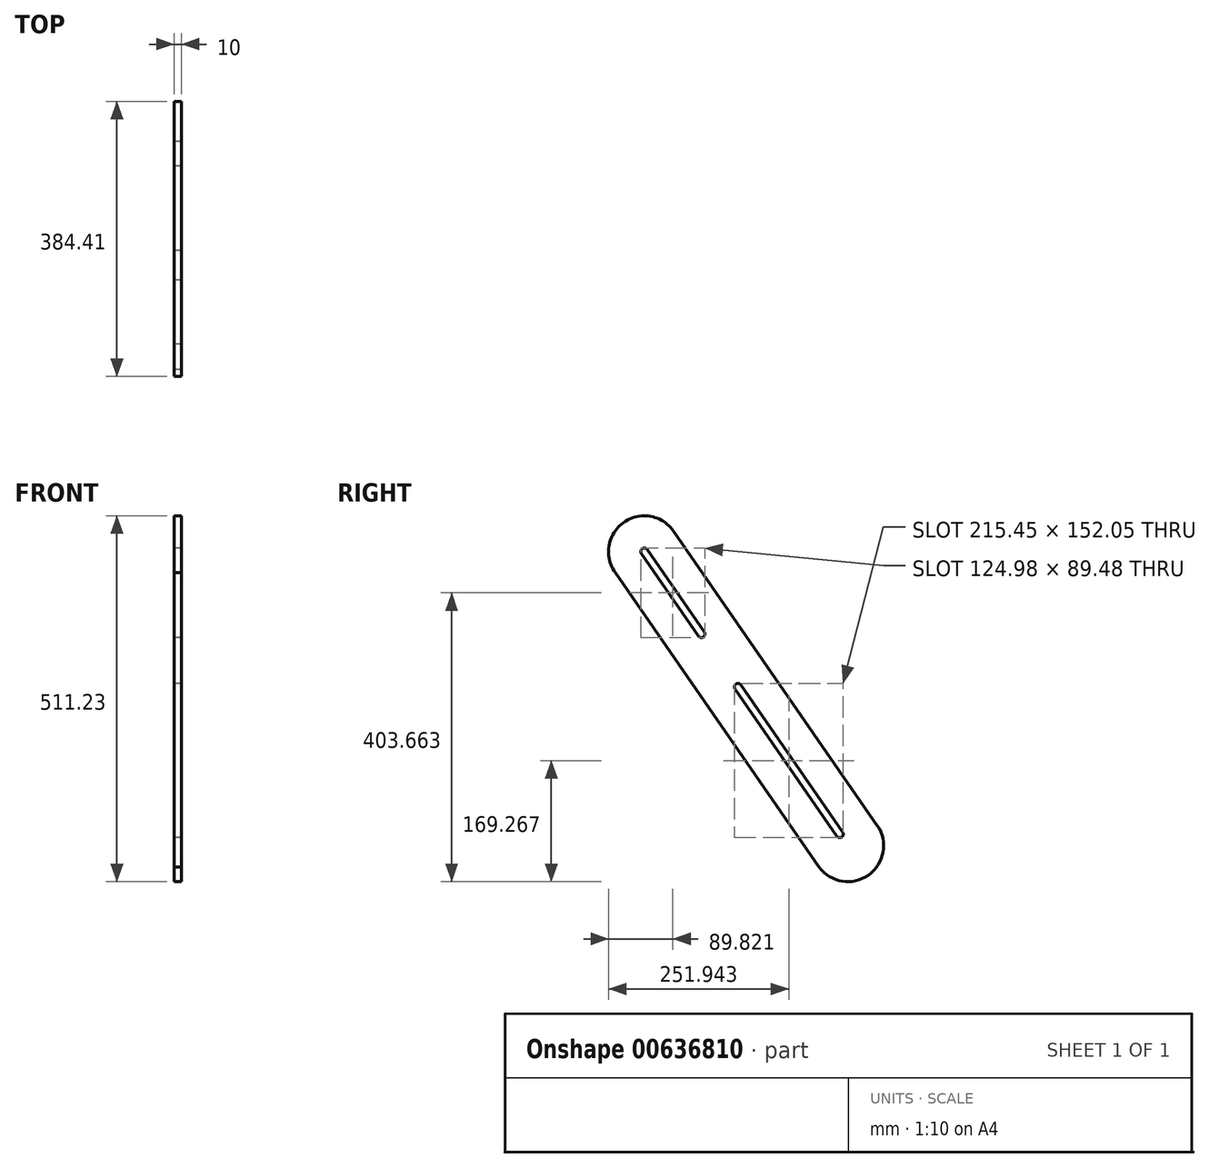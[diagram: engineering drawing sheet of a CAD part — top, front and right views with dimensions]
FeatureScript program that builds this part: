
annotation { "Feature Type Name" : "Feature", "Feature Type Description" : "" }
export const myFeature = defineFeature(function(context is Context, id is Id, definition is map)
    precondition{}
    {
        {
            var Q0;
            Q0=qCreatedBy(makeId("Right.planeOp"),FACE);
            var sketch = newSketch(context, id + "F0", { "sketchPlane" : qUnion([Q0])});
            skArc(sketch, "E0.0.0", {"start": v(-72.7, 193.08) * mm, "mid": v(-142.82, 205.37) * mm, "end": v(-154.18, 135.1) * mm});
            skLineSegment(sketch, "E0.0.1", {"start": v(-154.18, 135.1) * mm, "end": v(130.23, -276.13) * mm});
            skArc(sketch, "E0.0.2", {"start": v(130.23, -276.13) * mm, "mid": v(199.57, -287.34) * mm, "end": v(211.7, -218.16) * mm});
            skLineSegment(sketch, "E0.0.3", {"start": v(211.7, -218.16) * mm, "end": v(-72.7, 193.08) * mm});
            skLineSegment(sketch, "E1.0", {"start": v(-117.94, 161.79) * mm, "end": v(-38.3, 46.65) * mm});
            skLineSegment(sketch, "E2.0", {"start": v(-30.08, 52.34) * mm, "end": v(-109.72, 167.48) * mm});
            skArc(sketch, "E3.0", {"start": v(-109.72, 167.48) * mm, "mid": v(-116.67, 168.75) * mm, "end": v(-117.94, 161.79) * mm});
            skArc(sketch, "E4.0", {"start": v(-38.3, 46.65) * mm, "mid": v(-31.35, 45.38) * mm, "end": v(-30.08, 52.34) * mm});
            skArc(sketch, "E5.0", {"start": v(21.12, -21.68) * mm, "mid": v(14.16, -20.42) * mm, "end": v(12.9, -27.37) * mm});
            skLineSegment(sketch, "E6.0", {"start": v(12.9, -27.37) * mm, "end": v(155.1, -232.98) * mm});
            skLineSegment(sketch, "E7.0", {"start": v(163.33, -227.3) * mm, "end": v(21.12, -21.68) * mm});
            skArc(sketch, "E8.0", {"start": v(155.1, -232.98) * mm, "mid": v(162.06, -234.25) * mm, "end": v(163.33, -227.3) * mm});
            skSolve(sketch);
        }
        {
            var Q0;
            Q0=makeQuery(id+"F0.imprint","IMPRINT",FACE,{"disambiguationData":[TD([[makeQuery(id+"F0.imprint","IMPRINT",EDGE,{"derivedFrom":sQuery(id+"F0.wireOp",EDGE,"E0.0.0")}),1.0]])]});
            extrude(context, id + "F1", {"entities" : qUnion([Q0]), "depth" : 10 * mm, "offsetDistance" : 25 * mm});
        }
    });
